# Revit family: Shower-Showerhead-KOHLER-Coralais-K-11637
name_source: partatom
category: Plumbing Fixtures
revit_build: Autodesk Revit 2015 (Build: 20140606_1530(x64)
units: mm (PartAtom-declared; Revit-internal decimal feet)

## types (8) — shared parameters
ADA Compliant = No
Assembly Code = D2010700
CW Connection = No
Cold Water Inlet = Cold Water Inlet
Date Modified = 01/17/2019
Default Elevation = 0"
Drain Included = No
HW Connection = Yes
Height = 2 3/4"
Length = 3 15/16"
Manufacturer = KOHLER Co.
MasterFormat 1995 = 15410
MasterFormat 2004 = 22.41.23
Material = Premium Metal Construction
Pressure = 80.00 psi
Product Documentation Link = https://www.us.kohler.com
Product Name = Coralais
Product Page URL = http://www.us.kohler.com
Tempered Water Inlet = Tempered Water Inlet
URL = https://www.us.kohler.com
Vent Connection = No
Waste Connection = No
Waste Water Outlet = Waste Water Outlet
Width = 2 3/4"

## per-type parameters (varying)
| type | 11637 | 11637-E | 11637-G | 11637-H | Description | Finish | Flow Rate | Model | Type |
| 1.5 GPM, CP-Polished Chrome | No | No | No | Yes | 1.5 gpm single-function showerhead | Kohler-Metal-CP-Polished_Chrome | 2 GPM | 11637-H-CP | 1 |
| 1.5 GPM, G-Brushed Chrome | No | No | No | Yes | 1.5 gpm single-function showerhead | Kohler-Metal-G-Brushed_Chrome | 2 GPM | 11637-H-G | 2 |
| 1.75 GPM, CP-Polished Chrome | No | No | Yes | No | 1.75 gpm single-function showerhead | Kohler-Metal-CP-Polished_Chrome | 2 GPM | 11637-G-CP | 3 |
| 1.75 GPM, G-Brushed Chrome | No | No | Yes | No | 1.75 gpm single-function showerhead | Kohler-Metal-G-Brushed_Chrome | 2 GPM | 11637-G-G | 4 |
| 2 GPM, CP-Polished Chrome | No | Yes | No | No | 2.0 gpm single-function showerhead | Kohler-Metal-CP-Polished_Chrome | 2 GPM | 11637-E-CP | 5 |
| 2 GPM, G-Brushed Chrome | No | Yes | No | No | 2.0 gpm single-function showerhead | Kohler-Metal-G-Brushed_Chrome | 2 GPM | 11637-E-G | 6 |
| 2.5 GPM, CP-Polished Chrome | Yes | No | No | No | 2.5 gpm single-function showerhead | Kohler-Metal-CP-Polished_Chrome | 3 GPM | 11637-CP | 7 |
| 2.5 GPM, G-Brushed Chrome | Yes | No | No | No | 2.5 gpm single-function showerhead | Kohler-Metal-G-Brushed_Chrome | 3 GPM | 11637-G | 8 |

## geometry (parser evidence)
native form markers: Sweep x6
no freeform markers — native parametric forms only
